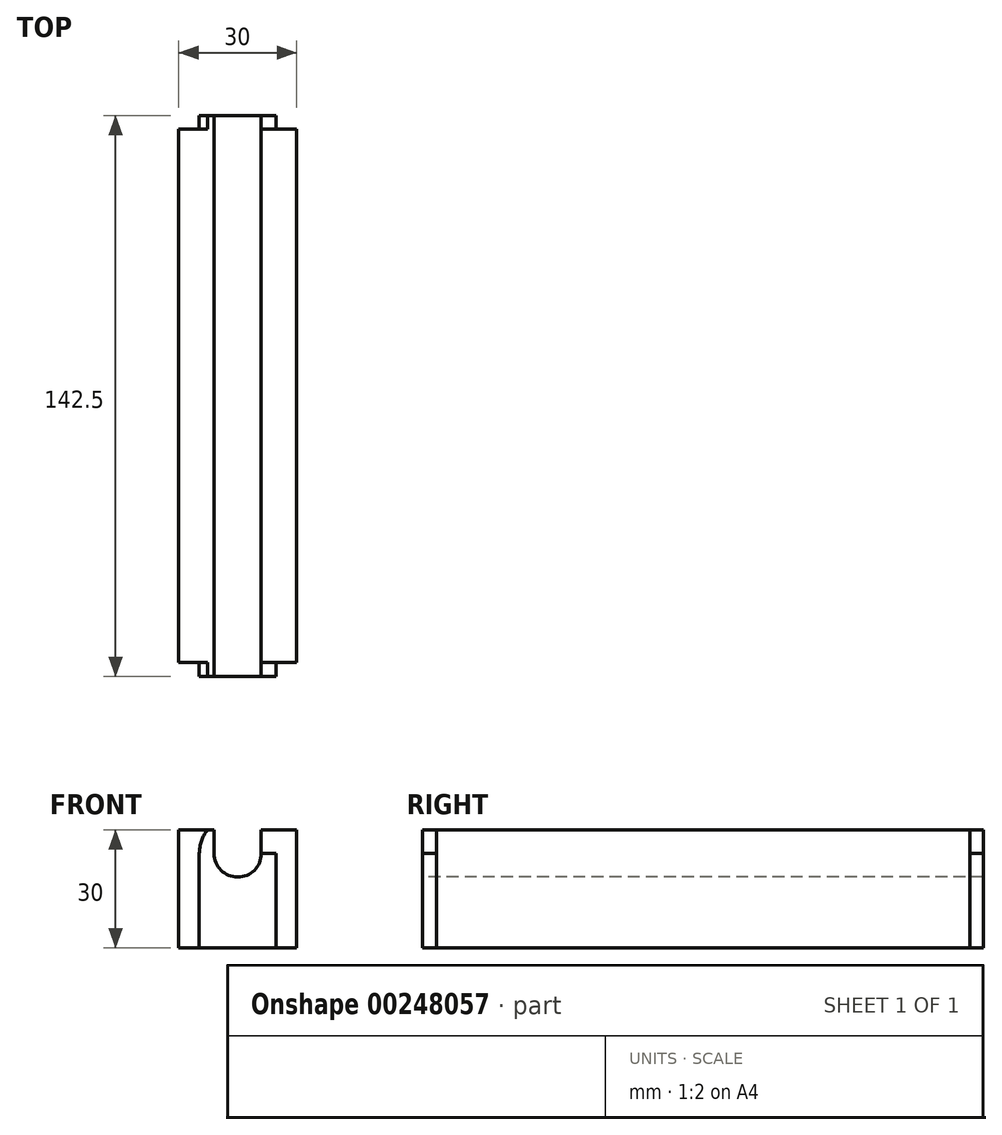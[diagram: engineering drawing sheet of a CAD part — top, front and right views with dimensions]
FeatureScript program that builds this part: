
annotation { "Feature Type Name" : "Feature", "Feature Type Description" : "" }
export const myFeature = defineFeature(function(context is Context, id is Id, definition is map)
    precondition{}
    {
        {
            var Q0;
            Q0=qCreatedBy(makeId("Front.planeOp"),FACE);
            var sketch = newSketch(context, id + "F0", { "sketchPlane" : qUnion([Q0])});
            skLineSegment(sketch, "E0.bottom", {"start": v(15, 15) * mm, "end": v(-15, 15) * mm});
            skLineSegment(sketch, "E0.top", {"start": v(15, -15) * mm, "end": v(-15, -15) * mm});
            skLineSegment(sketch, "E0.left", {"start": v(15, 15) * mm, "end": v(15, -15) * mm});
            skLineSegment(sketch, "E0.right", {"start": v(-15, 15) * mm, "end": v(-15, -15) * mm});
            skPoint(sketch, "E0.middle", {"position": v(0, 0) * mm});
            skSolve(sketch);
        }
        {
            var Q0;
            Q0 = qSketchRegion(id + "F0", true);
            extrude(context, id + "F1", {"entities" : qUnion([Q0]), "depth" : 71.25 * mm});
        }
        {
            var Q0;
            Q0=makeQuery(id+"F1.opExtrude","CAP_FACE",FACE,{"disambiguationData":[OSD([sQuery(id+"F0.wireOp",EDGE,"E0.bottom"),sQuery(id+"F0.wireOp",EDGE,"E0.top"),sQuery(id+"F0.wireOp",EDGE,"E0.left"),sQuery(id+"F0.wireOp",EDGE,"E0.right")])],"isStart":false});
            var sketch = newSketch(context, id + "F2", { "sketchPlane" : qUnion([Q0])});
            skLineSegment(sketch, "E1.0", {"start": v(14.49, 15) * mm, "end": v(-14.49, 15) * mm});
            skPoint(sketch, "E2.0.midPoint", {"position": v(0, 9) * mm});
            skPoint(sketch, "E3.orphan", {"position": v(-15, 15) * mm});
            skPoint(sketch, "E4.orphan", {"position": v(15, 15) * mm});
            skLineSegment(sketch, "E5", {"start": v(-14.49, 15) * mm, "end": v(14.49, 15) * mm});
            skArc(sketch, "E6", {"start": v(-6, 9) * mm, "mid": v(0, 3) * mm, "end": v(6, 9) * mm});
            skLineSegment(sketch, "E7", {"start": v(-6, 15) * mm, "end": v(-6, 9) * mm});
            skLineSegment(sketch, "E8", {"start": v(6, 15) * mm, "end": v(6, 9) * mm});
            skSolve(sketch);
        }
        {
            var Q0;
            Q0=makeQuery(id+"F2.imprint","IMPRINT",FACE,{"disambiguationData":[TD([[makeQuery(id+"F2.imprint","IMPRINT",EDGE,{"derivedFrom":sQuery(id+"F2.wireOp",EDGE,"E6")}),1.0]])]});
            extrude(context, id + "F3", {"entities" : qUnion([Q0]), "operationType" : NewBodyOperationType.REMOVE, "endBound" : BoundingType.THROUGH_ALL, "oppositeDirection" : true, "depth" : 25 * mm});
        }
        {
            var Q0;
            Q0=makeQuery(id+"F1.opExtrude","CAP_FACE",FACE,{"disambiguationData":[OSD([sQuery(id+"F0.wireOp",EDGE,"E0.bottom"),sQuery(id+"F0.wireOp",EDGE,"E0.top"),sQuery(id+"F0.wireOp",EDGE,"E0.left"),sQuery(id+"F0.wireOp",EDGE,"E0.right")])],"isStart":false});
            var sketch = newSketch(context, id + "F4", { "sketchPlane" : qUnion([Q0])});
            skLineSegment(sketch, "E9", {"start": v(-6, 15) * mm, "end": v(-6, 15) * mm});
            skArc(sketch, "E10", {"start": v(9.75, 9) * mm, "mid": v(0, 18.75) * mm, "end": v(-9.75, 9) * mm});
            skLineSegment(sketch, "E11", {"start": v(-9.75, -15) * mm, "end": v(-9.75, 9) * mm});
            skLineSegment(sketch, "E12.MirrorCS", {"start": v(9.75, -15) * mm, "end": v(9.75, 9) * mm});
            skLineSegment(sketch, "E13.bottom", {"start": v(-15, 15) * mm, "end": v(15, 15) * mm});
            skLineSegment(sketch, "E13.top", {"start": v(-15, 9) * mm, "end": v(15, 9) * mm});
            skLineSegment(sketch, "E13.left", {"start": v(-15, 15) * mm, "end": v(-15, 9) * mm});
            skLineSegment(sketch, "E13.right", {"start": v(15, 15) * mm, "end": v(15, 9) * mm});
            skSolve(sketch);
        }
        {
            var Q0;
            {var subQ0=sQuery(id+"F4.wireOp",EDGE,"E13.left");Q0=makeQuery(id+"F4.imprint","IMPRINT",FACE,{"disambiguationData":[TD([[makeQuery(id+"F4.imprint","IMPRINT",EDGE,{"derivedFrom":subQ0}),1.0]])]});}
            var Q1;
            {var subQ0=sQuery(id+"F4.wireOp",EDGE,"E13.bottom");var subQ1=sQuery(id+"F4.wireOp",EDGE,"E10");var subQ2=makeQuery(id+"F4.imprint","INTERSECT",VERTEX,{"disambiguationData":[OD(1.0)],"derivedFrom":[subQ1,subQ0]});Q1=makeQuery(id+"F4.imprint","IMPRINT",FACE,{"disambiguationData":[TD([[makeQuery(id+"F4.imprint","IMPRINT",EDGE,{"disambiguationData":[TD([[subQ2,-1.0]])],"derivedFrom":subQ1}),-1.0]])]});}
            var Q2;
            {var subQ5=sQuery(id+"F4.wireOp",EDGE,"E13.bottom");var subQ6=sQuery(id+"F4.wireOp",EDGE,"E10");var subQ7=makeQuery(id+"F4.imprint","INTERSECT",VERTEX,{"disambiguationData":[OD(0.0)],"derivedFrom":[subQ6,subQ5]});Q2=makeQuery(id+"F4.imprint","IMPRINT",FACE,{"disambiguationData":[TD([[makeQuery(id+"F4.imprint","IMPRINT",EDGE,{"disambiguationData":[TD([[subQ7,1.0]])],"derivedFrom":subQ6}),1.0]])]});}
            var Q3;
            {var subQ0=sQuery(id+"F4.wireOp",EDGE,"E13.bottom");var subQ1=sQuery(id+"F4.wireOp",EDGE,"E10");var subQ2=makeQuery(id+"F4.imprint","INTERSECT",VERTEX,{"disambiguationData":[OD(0.0)],"derivedFrom":[subQ1,subQ0]});Q3=makeQuery(id+"F4.imprint","IMPRINT",FACE,{"disambiguationData":[TD([[makeQuery(id+"F4.imprint","IMPRINT",EDGE,{"disambiguationData":[TD([[subQ2,1.0]])],"derivedFrom":subQ1}),-1.0]])]});}
            var Q4;
            {var subQ0=sQuery(id+"F4.wireOp",EDGE,"E13.right");Q4=makeQuery(id+"F4.imprint","IMPRINT",FACE,{"disambiguationData":[TD([[makeQuery(id+"F4.imprint","IMPRINT",EDGE,{"derivedFrom":subQ0}),-1.0]])]});}
            var Q5;
            {var subQ1=sQuery(id+"F4.wireOp",EDGE,"E10");var subQ3=makeQuery(id+"F3.boolean.opBoolean","COPY",EDGE,{"derivedFrom":makeQuery(id+"F3.opExtrude","CAP_EDGE",EDGE,{"disambiguationData":[OSD([sQuery(id+"F2.wireOp",EDGE,"wNhgUAUC-TQoo-c0yM-5687-1CzOaLSTJkm8")])],"isStart":true})});var subQ4=makeQuery(id+"F4.imprint","INTERSECT",VERTEX,{"derivedFrom":[subQ3,subQ1]});Q5=makeQuery(id+"F4.imprint","IMPRINT",FACE,{"disambiguationData":[TD([[makeQuery(id+"F4.imprint","IMPRINT",EDGE,{"disambiguationData":[TD([[subQ4,-1.0]])],"derivedFrom":subQ3}),1.0]])]});}
            var Q6;
            {var subQ1=sQuery(id+"F4.wireOp",EDGE,"E10");var subQ3=makeQuery(id+"F3.boolean.opBoolean","COPY",EDGE,{"derivedFrom":makeQuery(id+"F3.opExtrude","CAP_EDGE",EDGE,{"disambiguationData":[OSD([sQuery(id+"F2.wireOp",EDGE,"GRHWdFL9-lAlk-YMUy-zg4N-LFc6GhMVP314")])],"isStart":true})});var subQ4=makeQuery(id+"F4.imprint","INTERSECT",VERTEX,{"derivedFrom":[subQ3,subQ1]});Q6=makeQuery(id+"F4.imprint","IMPRINT",FACE,{"disambiguationData":[TD([[makeQuery(id+"F4.imprint","IMPRINT",EDGE,{"disambiguationData":[TD([[subQ4,-1.0]])],"derivedFrom":subQ3}),-1.0]])]});}
            var Q7;
            {var subQ0=sQuery(id+"F4.wireOp",EDGE,"E11");Q7=makeQuery(id+"F4.imprint","IMPRINT",FACE,{"disambiguationData":[TD([[makeQuery(id+"F4.imprint","IMPRINT",EDGE,{"derivedFrom":subQ0}),1.0]])]});}
            var Q8;
            {var subQ0=sQuery(id+"F4.wireOp",EDGE,"E12.MirrorCS");Q8=makeQuery(id+"F4.imprint","IMPRINT",FACE,{"disambiguationData":[TD([[makeQuery(id+"F4.imprint","IMPRINT",EDGE,{"derivedFrom":subQ0}),-1.0]])]});}
            var Q9;
            {var subQ5=makeQuery(id+"F3.boolean.opBoolean","COPY",EDGE,{"derivedFrom":makeQuery(id+"F3.opExtrude","CAP_EDGE",EDGE,{"disambiguationData":[OSD([sQuery(id+"F2.wireOp",EDGE,"E7")])],"isStart":true})});Q9=makeQuery(id+"F4.imprint","IMPRINT",FACE,{"disambiguationData":[TD([[makeQuery(id+"F4.imprint","IMPRINT",EDGE,{"derivedFrom":subQ5}),-1.0]])]});}
            extrude(context, id + "F5", {"entities" : qUnion([Q0, Q1, Q2, Q3, Q4, Q5, Q6, Q7, Q8, Q9]), "operationType" : NewBodyOperationType.REMOVE, "oppositeDirection" : true, "depth" : 3.5 * mm});
        }
        {
            var Q0;
            Q0=makeQuery(id+"F1.opExtrude","SWEPT_BODY",BODY,{"disambiguationData":[OSD([sQuery(id+"F0.wireOp",EDGE,"E0.bottom"),sQuery(id+"F0.wireOp",EDGE,"E0.top"),sQuery(id+"F0.wireOp",EDGE,"E0.left"),sQuery(id+"F0.wireOp",EDGE,"E0.right")])]});
            var Q1;
            Q1=qCreatedBy(makeId("Front.planeOp"),FACE);
            mirror(context, id + "F6", {"operationType" : NewBodyOperationType.ADD, "entities" : qUnion([Q0]), "mirrorPlane" : qUnion([Q1])});
        }
    });
